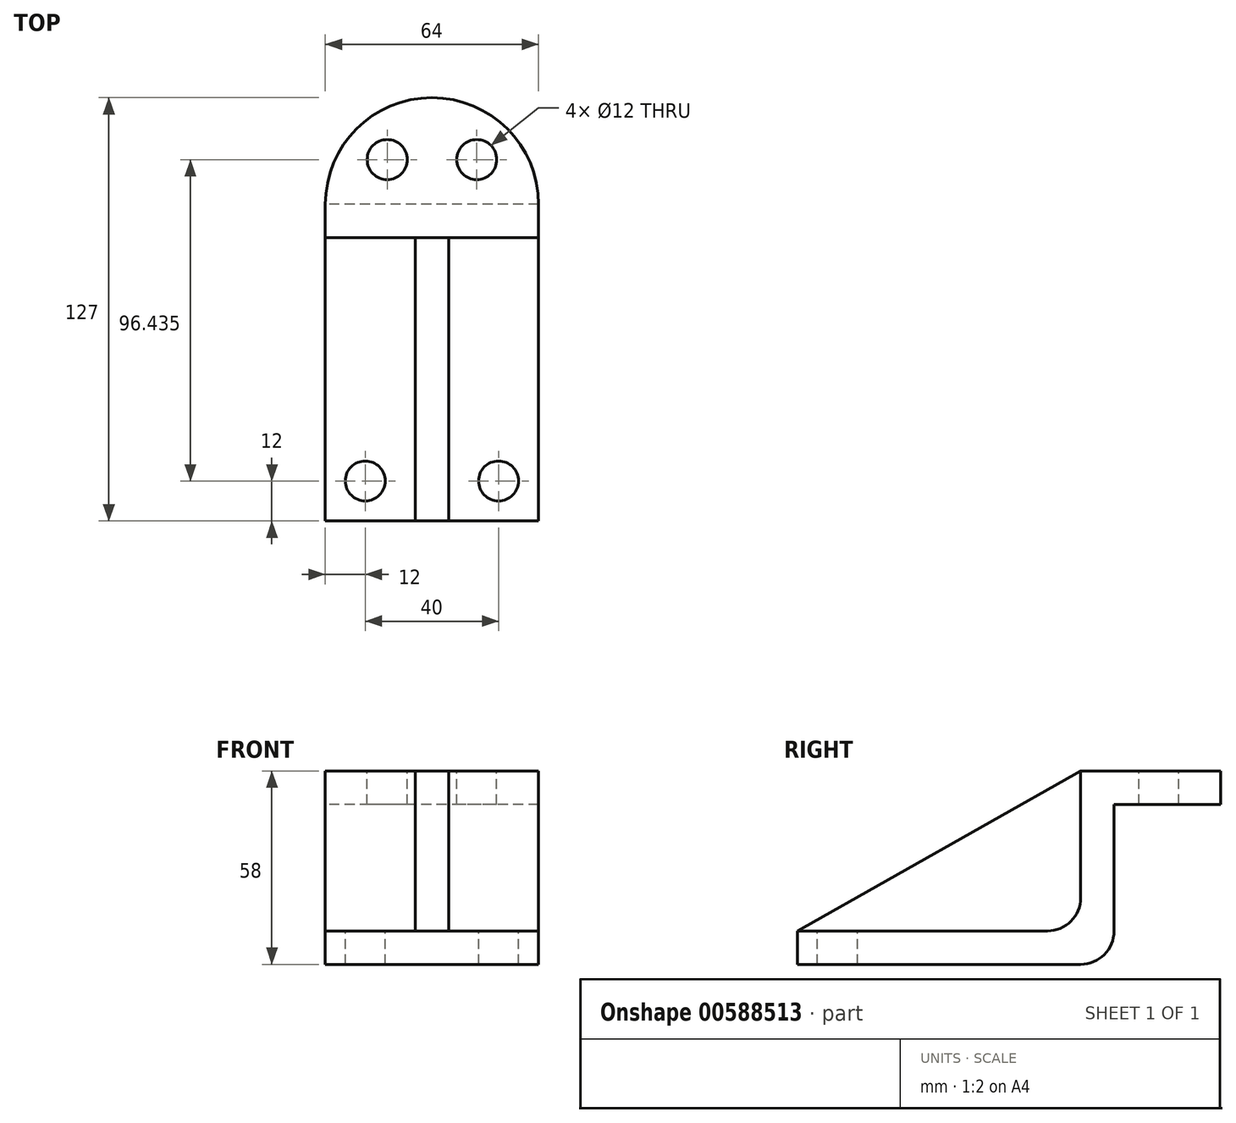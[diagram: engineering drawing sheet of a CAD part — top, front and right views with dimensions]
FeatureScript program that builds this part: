
annotation { "Feature Type Name" : "Feature", "Feature Type Description" : "" }
export const myFeature = defineFeature(function(context is Context, id is Id, definition is map)
    precondition{}
    {
        {
            var Q0;
            Q0=qCreatedBy(makeId("Right.planeOp"),FACE);
            var sketch = newSketch(context, id + "F0", { "sketchPlane" : qUnion([Q0])});
            skLineSegment(sketch, "E0", {"start": v(0, 0) * mm, "end": v(85, 48) * mm});
            skLineSegment(sketch, "E1", {"start": v(85, 48) * mm, "end": v(85, 10) * mm});
            skLineSegment(sketch, "E2", {"start": v(75, 0) * mm, "end": v(0, 0) * mm});
            skLineSegment(sketch, "E3", {"start": v(0, 0) * mm, "end": v(0, -10) * mm});
            skLineSegment(sketch, "E4", {"start": v(0, -10) * mm, "end": v(85, -10) * mm});
            skLineSegment(sketch, "E5", {"start": v(95, 0) * mm, "end": v(95, 38) * mm});
            skLineSegment(sketch, "E6", {"start": v(95, 38) * mm, "end": v(127, 38) * mm});
            skLineSegment(sketch, "E7", {"start": v(127, 38) * mm, "end": v(127, 48) * mm});
            skLineSegment(sketch, "E8", {"start": v(127, 48) * mm, "end": v(85, 48) * mm});
            skPoint(sketch, "E9.visualSharp", {"position": v(85, 0) * mm});
            skArc(sketch, "E9.filletArc", {"start": v(75, 0) * mm, "mid": v(82.07, 2.93) * mm, "end": v(85, 10) * mm});
            skPoint(sketch, "E10.visualSharp", {"position": v(95, -10) * mm});
            skArc(sketch, "E10.filletArc", {"start": v(85, -10) * mm, "mid": v(92.07, -7.07) * mm, "end": v(95, 0) * mm});
            skSolve(sketch);
        }
        {
            var Q0;
            Q0=makeQuery(id+"F0.imprint","IMPRINT",FACE,{"disambiguationData":[TD([[makeQuery(id+"F0.imprint","IMPRINT",EDGE,{"derivedFrom":sQuery(id+"F0.wireOp",EDGE,"E0")}),-1.0]])]});
            var Q1;
            Q1=makeQuery(id+"F0.imprint","IMPRINT",FACE,{"disambiguationData":[TD([[makeQuery(id+"F0.imprint","IMPRINT",EDGE,{"derivedFrom":sQuery(id+"F0.wireOp",EDGE,"E1")}),1.0]])]});
            extrude(context, id + "F1", {"entities" : qUnion([Q0, Q1]), "depth" : 10 * mm, "offsetDistance" : 25 * mm, "symmetric" : true});
        }
        {
            var Q0;
            Q0=makeQuery(id+"F0.imprint","IMPRINT",FACE,{"disambiguationData":[TD([[makeQuery(id+"F0.imprint","IMPRINT",EDGE,{"derivedFrom":sQuery(id+"F0.wireOp",EDGE,"E1")}),1.0]])]});
            extrude(context, id + "F2", {"entities" : qUnion([Q0]), "operationType" : NewBodyOperationType.ADD, "depth" : 64 * mm, "offsetDistance" : 25 * mm, "symmetric" : true});
        }
        {
            var Q0;
            {var subQ0=sQuery(id+"F0.wireOp",EDGE,"E8");Q0=makeQuery(id+"F2.boolean.opBoolean","MERGE",FACE,{"derivedFrom":[makeQuery(id+"F1.opExtrude","SWEPT_FACE",FACE,{"disambiguationData":[OSD([subQ0])]}),makeQuery(id+"F2.opExtrude","SWEPT_FACE",FACE,{"disambiguationData":[OSD([subQ0])]})]});}
            var sketch = newSketch(context, id + "F3", { "sketchPlane" : qUnion([Q0])});
            skSolve(sketch);
        }
        {
            var Q0;
            {var subQ0=sQuery(id+"F0.wireOp",EDGE,"E8");Q0=makeQuery(id+"F3.imprint","IMPRINT",FACE,{"disambiguationData":[TD([[makeQuery(id+"F3.imprint","IMPRINT",EDGE,{"derivedFrom":makeQuery(id+"F2.opExtrude","CAP_EDGE",EDGE,{"disambiguationData":[OSD([subQ0])],"isStart":true})}),1.0]])]});}
            var sketch = newSketch(context, id + "F4", { "sketchPlane" : qUnion([Q0])});
            skArc(sketch, "E11", {"start": v(32, 95) * mm, "mid": v(0, 127) * mm, "end": v(-32, 95) * mm});
            skLineSegment(sketch, "E12", {"start": v(32, 95) * mm, "end": v(32, 127) * mm});
            skLineSegment(sketch, "E13", {"start": v(32, 127) * mm, "end": v(-32, 127) * mm});
            skLineSegment(sketch, "E14", {"start": v(-32, 127) * mm, "end": v(-32, 95) * mm});
            skCircle(sketch, "E15", {"center": v(0, 95) * mm, "radius": 19 * mm, "construction": true});
            skCircle(sketch, "E16", {"center": v(-13.44, 108.44) * mm, "radius": 6 * mm});
            skCircle(sketch, "E17", {"center": v(13.44, 108.44) * mm, "radius": 6 * mm});
            skLineSegment(sketch, "E18", {"start": v(13.44, 108.44) * mm, "end": v(0, 95) * mm, "construction": true});
            skLineSegment(sketch, "E19", {"start": v(0, 95) * mm, "end": v(-13.44, 108.44) * mm, "construction": true});
            skCircle(sketch, "E20", {"center": v(20, 12) * mm, "radius": 6 * mm});
            skCircle(sketch, "E21", {"center": v(-20, 12) * mm, "radius": 6 * mm});
            skSolve(sketch);
        }
        {
            var Q0;
            {var subQ0=sQuery(id+"F4.wireOp",EDGE,"E14");Q0=makeQuery(id+"F4.imprint","IMPRINT",FACE,{"disambiguationData":[TD([[makeQuery(id+"F4.imprint","IMPRINT",EDGE,{"derivedFrom":subQ0}),1.0]])]});}
            var Q1;
            {var subQ0=sQuery(id+"F4.wireOp",EDGE,"E12");Q1=makeQuery(id+"F4.imprint","IMPRINT",FACE,{"disambiguationData":[TD([[makeQuery(id+"F4.imprint","IMPRINT",EDGE,{"derivedFrom":subQ0}),-1.0]])]});}
            var Q2;
            Q2=makeQuery(id+"F4.imprint","IMPRINT",FACE,{"disambiguationData":[TD([[makeQuery(id+"F4.imprint","IMPRINT",EDGE,{"derivedFrom":sQuery(id+"F4.wireOp",EDGE,"E17")}),1.0]])]});
            var Q3;
            Q3=makeQuery(id+"F4.imprint","IMPRINT",FACE,{"disambiguationData":[TD([[makeQuery(id+"F4.imprint","IMPRINT",EDGE,{"derivedFrom":sQuery(id+"F4.wireOp",EDGE,"E16")}),1.0]])]});
            var Q4;
            Q4=makeQuery(id+"F4.imprint","IMPRINT",FACE,{"disambiguationData":[TD([[makeQuery(id+"F4.imprint","IMPRINT",EDGE,{"derivedFrom":sQuery(id+"F4.wireOp",EDGE,"E21")}),1.0]])]});
            var Q5;
            Q5=makeQuery(id+"F4.imprint","IMPRINT",FACE,{"disambiguationData":[TD([[makeQuery(id+"F4.imprint","IMPRINT",EDGE,{"derivedFrom":sQuery(id+"F4.wireOp",EDGE,"E20")}),1.0]])]});
            extrude(context, id + "F5", {"entities" : qUnion([Q0, Q1, Q2, Q3, Q4, Q5]), "operationType" : NewBodyOperationType.REMOVE, "endBound" : BoundingType.THROUGH_ALL, "oppositeDirection" : true, "depth" : 25 * mm, "offsetDistance" : 25 * mm});
        }
    });
